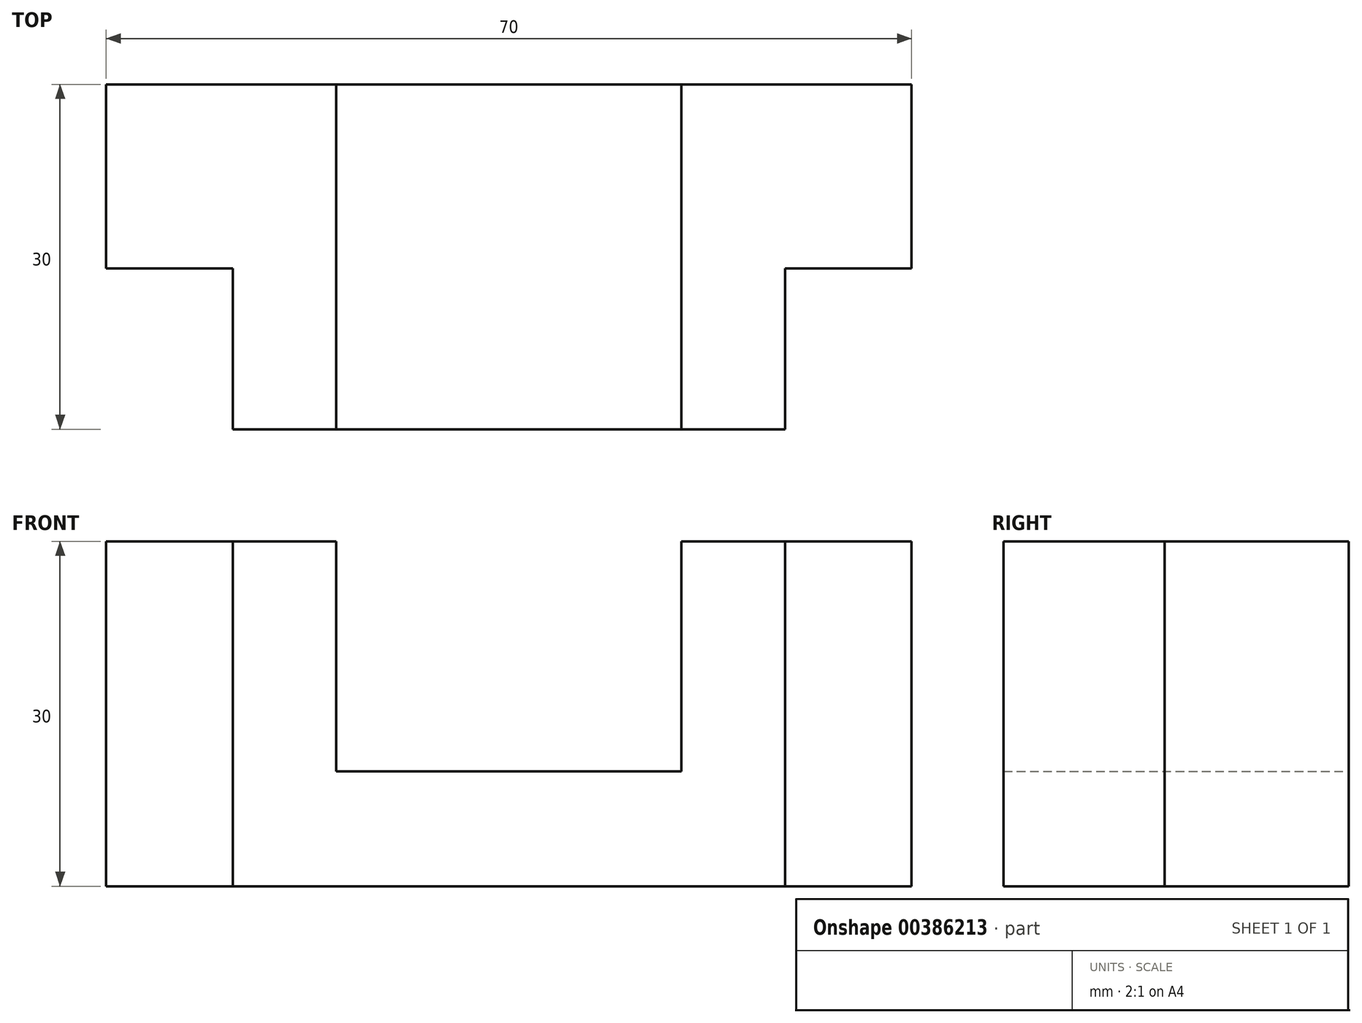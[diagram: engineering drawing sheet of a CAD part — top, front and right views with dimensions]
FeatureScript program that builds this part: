
annotation { "Feature Type Name" : "Feature", "Feature Type Description" : "" }
export const myFeature = defineFeature(function(context is Context, id is Id, definition is map)
    precondition{}
    {
        {
            var Q0;
            Q0=qCreatedBy(makeId("Front.planeOp"),FACE);
            var sketch = newSketch(context, id + "F0", { "sketchPlane" : qUnion([Q0])});
            skLineSegment(sketch, "E0.top", {"start": v(-24, -16.25) * mm, "end": v(24, -16.25) * mm});
            skLineSegment(sketch, "E0.left", {"start": v(-24, 13.75) * mm, "end": v(-24, -16.25) * mm});
            skLineSegment(sketch, "E0.right", {"start": v(24, 13.75) * mm, "end": v(24, -16.25) * mm});
            skLineSegment(sketch, "E1.top", {"start": v(-15, -6.25) * mm, "end": v(15, -6.25) * mm});
            skLineSegment(sketch, "E1.left", {"start": v(-15, 13.75) * mm, "end": v(-15, -6.25) * mm});
            skLineSegment(sketch, "E1.right", {"start": v(15, 13.75) * mm, "end": v(15, -6.25) * mm});
            skLineSegment(sketch, "E2.trimOffspring", {"start": v(15, 13.75) * mm, "end": v(24, 13.75) * mm});
            skLineSegment(sketch, "E3", {"start": v(-24, 13.75) * mm, "end": v(-15, 13.75) * mm});
            skLineSegment(sketch, "E4.bottom", {"start": v(24, 13.75) * mm, "end": v(35, 13.75) * mm});
            skLineSegment(sketch, "E4.top", {"start": v(24, -16.25) * mm, "end": v(35, -16.25) * mm});
            skLineSegment(sketch, "E4.right", {"start": v(35, 13.75) * mm, "end": v(35, -16.25) * mm});
            skLineSegment(sketch, "E5.bottom", {"start": v(-24, 13.75) * mm, "end": v(-35, 13.75) * mm});
            skLineSegment(sketch, "E5.top", {"start": v(-24, -16.25) * mm, "end": v(-35, -16.25) * mm});
            skLineSegment(sketch, "E5.right", {"start": v(-35, 13.75) * mm, "end": v(-35, -16.25) * mm});
            skSolve(sketch);
        }
        {
            var Q0;
            Q0=makeQuery(id+"F0.imprint","IMPRINT",FACE,{"disambiguationData":[TD([[makeQuery(id+"F0.imprint","IMPRINT",EDGE,{"derivedFrom":sQuery(id+"F0.wireOp",EDGE,"E0.top")}),1.0]])]});
            extrude(context, id + "F1", {"entities" : qUnion([Q0]), "depth" : 30 * mm});
        }
        {
            var Q0;
            Q0 = qSketchRegion(id + "F0", true);
            extrude(context, id + "F2", {"entities" : qUnion([Q0]), "operationType" : NewBodyOperationType.ADD, "depth" : 16 * mm});
        }
    });
